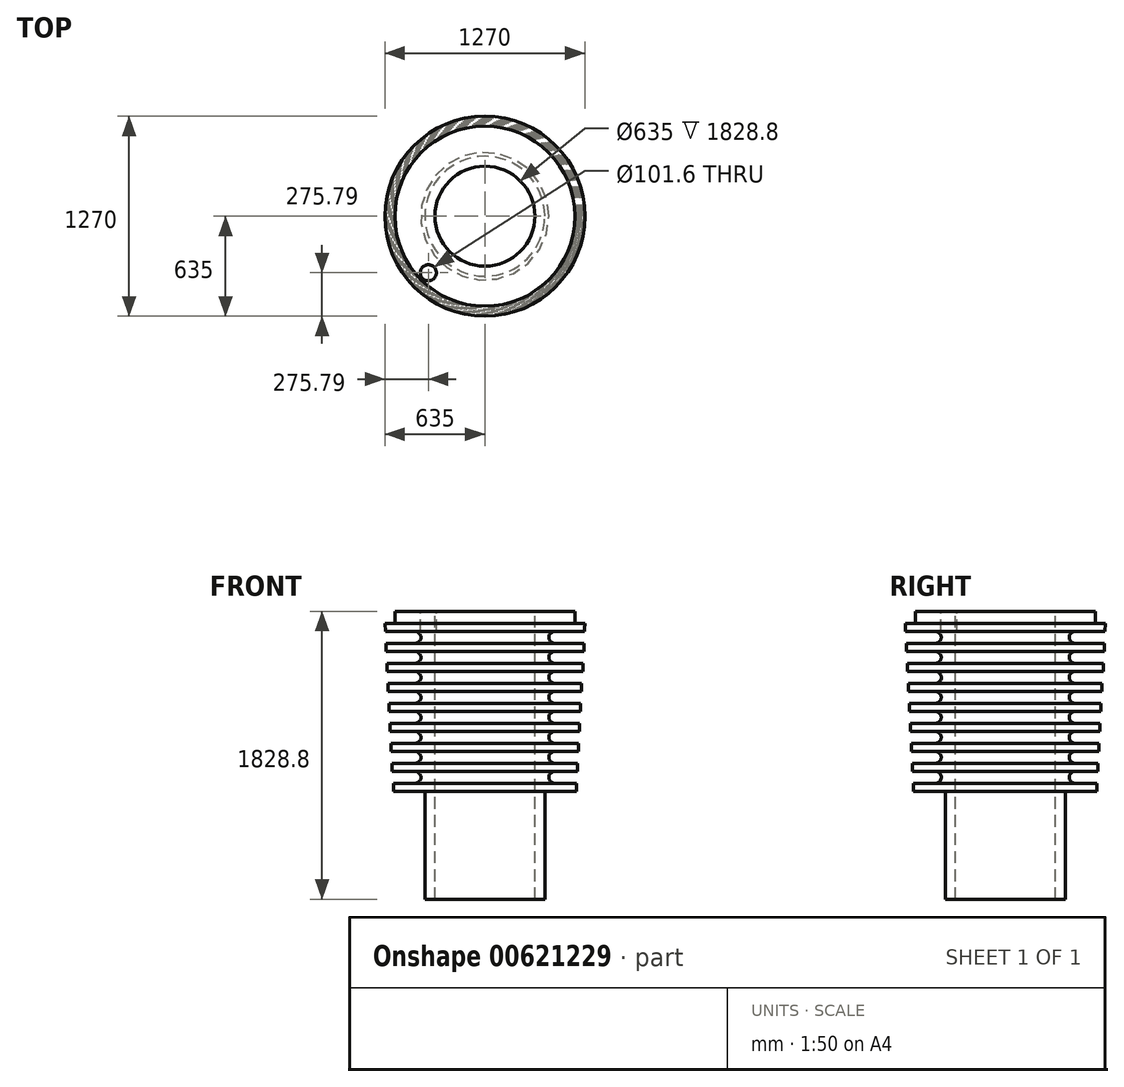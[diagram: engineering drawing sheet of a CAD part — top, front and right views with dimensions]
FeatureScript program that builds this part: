
annotation { "Feature Type Name" : "Feature", "Feature Type Description" : "" }
export const myFeature = defineFeature(function(context is Context, id is Id, definition is map)
    precondition{}
    {
        {
            var Q0;
            Q0=qCreatedBy(makeId("Front.planeOp"),FACE);
            var sketch = newSketch(context, id + "F0", { "sketchPlane" : qUnion([Q0])});
            skLineSegment(sketch, "E0", {"start": v(0, 633.72) * mm, "end": v(0, -1828.8) * mm});
            skLineSegment(sketch, "E1", {"start": v(317.5, 0) * mm, "end": v(571.5, 0) * mm});
            skLineSegment(sketch, "E2", {"start": v(571.5, 0) * mm, "end": v(571.5, -76.2) * mm});
            skLineSegment(sketch, "E3", {"start": v(317.5, -76.2) * mm, "end": v(635, -76.2) * mm});
            skLineSegment(sketch, "E4", {"start": v(635, -76.2) * mm, "end": v(635, -127) * mm});
            skLineSegment(sketch, "E5", {"start": v(317.5, 0) * mm, "end": v(317.5, -76.2) * mm});
            skLineSegment(sketch, "E6", {"start": v(317.5, 0) * mm, "end": v(381, 0) * mm});
            skLineSegment(sketch, "E7", {"start": v(381, -1143) * mm, "end": v(579.1, -1143) * mm});
            skPoint(sketch, "E8", {"position": v(0, -1143) * mm});
            skPoint(sketch, "E9.orphan", {"position": v(-1281.27, -1143) * mm});
            skLineSegment(sketch, "E10", {"start": v(317.5, -76.2) * mm, "end": v(317.5, -1828.8) * mm});
            skLineSegment(sketch, "E11", {"start": v(317.5, -1828.8) * mm, "end": v(381, -1828.8) * mm});
            skLineSegment(sketch, "E12.trimOffspring", {"start": v(381, -1143) * mm, "end": v(381, -1828.8) * mm});
            skPoint(sketch, "E13.orphan", {"position": v(0, 0) * mm});
            skPoint(sketch, "E14.orphan", {"position": v(0, -76.2) * mm});
            skLineSegment(sketch, "E15", {"start": v(381, -1524) * mm, "end": v(431.8, -1524) * mm});
            skLineSegment(sketch, "E16", {"start": v(431.8, -1524) * mm, "end": v(431.8, -1651) * mm});
            skLineSegment(sketch, "E17", {"start": v(431.8, -1651) * mm, "end": v(381, -1651) * mm});
            skLineSegment(sketch, "E18", {"start": v(635, -76.2) * mm, "end": v(632.34, -127) * mm});
            skPoint(sketch, "E19.orphan", {"position": v(571.5, -1287.85) * mm});
            skPoint(sketch, "E20.orphan", {"position": v(1281.27, -1143) * mm});
            skLineSegment(sketch, "E21", {"start": v(444.5, 915.87) * mm, "end": v(444.5, -127) * mm, "construction": true});
            skLineSegment(sketch, "E22", {"start": v(635, -127) * mm, "end": v(444.5, -127) * mm});
            skLineSegment(sketch, "E23", {"start": v(444.5, -203.2) * mm, "end": v(628.34, -203.2) * mm});
            skLineSegment(sketch, "E24", {"start": v(628.34, -203.2) * mm, "end": v(444.5, -203.2) * mm});
            skLineSegment(sketch, "E25", {"start": v(628.34, -203.2) * mm, "end": v(628.34, -254) * mm});
            skLineSegment(sketch, "E26", {"start": v(444.5, -254) * mm, "end": v(628.34, -254) * mm});
            skPoint(sketch, "E27.orphan", {"position": v(628.34, -353.57) * mm});
            skLineSegment(sketch, "E28", {"start": v(621.69, -330.2) * mm, "end": v(444.5, -330.2) * mm});
            skPoint(sketch, "E29.orphan", {"position": v(621.69, -330.2) * mm});
            skLineSegment(sketch, "E30", {"start": v(621.69, -330.2) * mm, "end": v(621.69, -381) * mm});
            skLineSegment(sketch, "E31", {"start": v(621.69, -381) * mm, "end": v(444.5, -381) * mm});
            skLineSegment(sketch, "E32", {"start": v(615.03, -457.2) * mm, "end": v(444.5, -457.2) * mm});
            skPoint(sketch, "E33.orphan", {"position": v(621.69, -457.2) * mm});
            skLineSegment(sketch, "E34", {"start": v(615.03, -457.2) * mm, "end": v(615.03, -508) * mm});
            skLineSegment(sketch, "E35", {"start": v(615.03, -508) * mm, "end": v(444.5, -508) * mm});
            skLineSegment(sketch, "E36", {"start": v(608.38, -584.2) * mm, "end": v(444.5, -584.2) * mm});
            skPoint(sketch, "E37.start.orphan", {"position": v(612.37, -508) * mm});
            skPoint(sketch, "E38.orphan", {"position": v(612.37, -584.2) * mm});
            skLineSegment(sketch, "E39", {"start": v(608.38, -584.2) * mm, "end": v(608.38, -635) * mm});
            skLineSegment(sketch, "E40", {"start": v(608.38, -635) * mm, "end": v(444.5, -635) * mm});
            skLineSegment(sketch, "E41", {"start": v(601.72, -711.2) * mm, "end": v(444.5, -711.2) * mm});
            skPoint(sketch, "E42.orphan", {"position": v(605.71, -635) * mm});
            skLineSegment(sketch, "E43", {"start": v(601.72, -711.2) * mm, "end": v(601.72, -762) * mm});
            skLineSegment(sketch, "E44", {"start": v(601.72, -762) * mm, "end": v(444.5, -762) * mm});
            skLineSegment(sketch, "E45", {"start": v(595.07, -838.2) * mm, "end": v(444.5, -838.2) * mm});
            skPoint(sketch, "E46.orphan", {"position": v(599.06, -838.2) * mm});
            skPoint(sketch, "E47.trimOffspring.end.orphan", {"position": v(599.06, -762) * mm});
            skLineSegment(sketch, "E48", {"start": v(595.07, -838.2) * mm, "end": v(595.07, -889) * mm});
            skLineSegment(sketch, "E49", {"start": v(595.07, -889) * mm, "end": v(444.5, -889) * mm});
            skLineSegment(sketch, "E50", {"start": v(592.4, -965.2) * mm, "end": v(444.5, -965.2) * mm});
            skPoint(sketch, "E51.orphan", {"position": v(592.4, -889) * mm});
            skLineSegment(sketch, "E52", {"start": v(588.4, -965.2) * mm, "end": v(588.4, -1016) * mm});
            skLineSegment(sketch, "E53", {"start": v(588.4, -1016) * mm, "end": v(444.5, -1016) * mm});
            skLineSegment(sketch, "E54", {"start": v(581.75, -1092.2) * mm, "end": v(444.5, -1092.2) * mm});
            skPoint(sketch, "E55.start.orphan", {"position": v(585.75, -1016) * mm});
            skPoint(sketch, "E56.orphan", {"position": v(585.75, -1092.2) * mm});
            skLineSegment(sketch, "E57", {"start": v(581.75, -1092.2) * mm, "end": v(581.75, -1143) * mm});
            skLineSegment(sketch, "E58", {"start": v(581.75, -1143) * mm, "end": v(444.5, -1143) * mm});
            skArc(sketch, "E59", {"start": v(444.5, -127) * mm, "mid": v(406.4, -165.1) * mm, "end": v(444.5, -203.2) * mm});
            skArc(sketch, "E60", {"start": v(444.5, -254) * mm, "mid": v(406.4, -292.1) * mm, "end": v(444.5, -330.2) * mm});
            skLineSegment(sketch, "E61.trimOffspring", {"start": v(444.5, -330.2) * mm, "end": v(444.5, -381) * mm, "construction": true});
            skArc(sketch, "E62", {"start": v(444.5, -381) * mm, "mid": v(406.4, -419.1) * mm, "end": v(444.5, -457.2) * mm});
            skLineSegment(sketch, "E63.trimOffspring", {"start": v(444.5, -457.2) * mm, "end": v(444.5, -508) * mm, "construction": true});
            skArc(sketch, "E64", {"start": v(444.5, -635) * mm, "mid": v(406.4, -673.1) * mm, "end": v(444.5, -711.2) * mm});
            skLineSegment(sketch, "E65.trimOffspring", {"start": v(444.5, -711.2) * mm, "end": v(444.5, -762) * mm, "construction": true});
            skArc(sketch, "E66", {"start": v(444.5, -508) * mm, "mid": v(406.4, -546.1) * mm, "end": v(444.5, -584.2) * mm});
            skLineSegment(sketch, "E67.trimOffspring", {"start": v(444.5, -584.2) * mm, "end": v(444.5, -635) * mm, "construction": true});
            skPoint(sketch, "E68.orphan", {"position": v(605.71, -711.2) * mm});
            skArc(sketch, "E69", {"start": v(444.5, -762) * mm, "mid": v(406.4, -800.1) * mm, "end": v(444.5, -838.2) * mm});
            skLineSegment(sketch, "E70.trimOffspring", {"start": v(444.5, -838.2) * mm, "end": v(444.5, -889) * mm, "construction": true});
            skArc(sketch, "E71", {"start": v(444.5, -889) * mm, "mid": v(406.4, -927.1) * mm, "end": v(444.5, -965.2) * mm});
            skLineSegment(sketch, "E72.trimOffspring", {"start": v(444.5, -965.2) * mm, "end": v(444.5, -1016) * mm, "construction": true});
            skArc(sketch, "E73", {"start": v(444.5, -1016) * mm, "mid": v(406.4, -1054.1) * mm, "end": v(444.5, -1092.2) * mm});
            skLineSegment(sketch, "E74.trimOffspring", {"start": v(444.5, -1092.2) * mm, "end": v(444.5, -2531.9) * mm, "construction": true});
            skSolve(sketch);
        }
        {
            var Q0;
            {var subQ4=sQuery(id+"F0.wireOp",EDGE,"E7");Q0=makeQuery(id+"F0.imprint","IMPRINT",FACE,{"disambiguationData":[TD([[makeQuery(id+"F0.imprint","IMPRINT",EDGE,{"derivedFrom":subQ4}),1.0]])]});}
            var Q1;
            Q1=makeQuery(id+"F0.imprint","IMPRINT",FACE,{"disambiguationData":[TD([[makeQuery(id+"F0.imprint","IMPRINT",EDGE,{"derivedFrom":sQuery(id+"F0.wireOp",EDGE,"E1")}),-1.0]])]});
            var Q2;
            Q2=sQuery(id+"F0.wireOp",EDGE,"E0");
            revolve(context, id + "F1", {"entities" : qUnion([Q0, Q1]), "axis" : qUnion([Q2]), "revolveType" : RevolveType.FULL});
        }
        {
            var Q0;
            Q0=qCreatedBy(makeId("Top.planeOp"),FACE);
            var sketch = newSketch(context, id + "F2", { "sketchPlane" : qUnion([Q0])});
            skCircle(sketch, "E75", {"center": v(0, 0) * mm, "radius": 508 * mm, "construction": true});
            skLineSegment(sketch, "E76", {"start": v(0, 0) * mm, "end": v(-508, 0) * mm, "construction": true});
            skLineSegment(sketch, "E77", {"start": v(0, 0) * mm, "end": v(0, -508) * mm, "construction": true});
            skLineSegment(sketch, "E78", {"start": v(0, 0) * mm, "end": v(-359.21, -359.21) * mm, "construction": true});
            skCircle(sketch, "E79", {"center": v(-359.21, -359.21) * mm, "radius": 50.8 * mm});
            skSolve(sketch);
        }
        {
            var Q0;
            Q0=makeQuery(id+"F2.imprint","IMPRINT",FACE,{"disambiguationData":[TD([[makeQuery(id+"F2.imprint","IMPRINT",EDGE,{"derivedFrom":sQuery(id+"F2.wireOp",EDGE,"E79")}),1.0]])]});
            var Q1;
            Q1=makeQuery(id+"F1.opRevolve","SWEPT_FACE",FACE,{"disambiguationData":[OSD([sQuery(id+"F0.wireOp",EDGE,"E22")])]});
            extrude(context, id + "F3", {"entities" : qUnion([Q0]), "operationType" : NewBodyOperationType.REMOVE, "endBound" : BoundingType.UP_TO_SURFACE, "oppositeDirection" : true, "depth" : 25.4 * mm, "endBoundEntityFace" : qUnion([Q1]), "offsetDistance" : 25.4 * mm});
        }
    });
